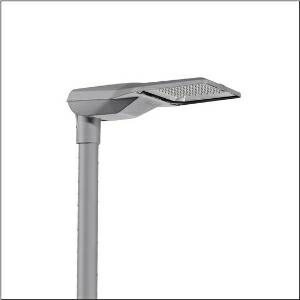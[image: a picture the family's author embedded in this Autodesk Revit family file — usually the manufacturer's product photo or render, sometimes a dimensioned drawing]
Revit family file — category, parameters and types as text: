
# Revit family: streetlight_sl_21_iq_midi___stw1_0a_5xe3e41d08nb_e017
name_source: partatom
category: Lighting Fixtures
units: mm (PartAtom-declared; Revit-internal decimal feet)

## family parameters
Cut with Voids When Loaded = No
Host = Face
Light Source = No
Part Type = Normal
Room Calculation Point = No
Round Connector Dimension = Use Diameter
Shared = No

## types (1)
- --- (1 x LED, 24250 lm, 155.5 W, 4000K)
    Apparent Load = 155 VA
    CIE Flux Codes = 39 75 98 100 100
    Color Rendering = 70
    Color Temperature = 4000K
    Default Elevation = 1800 mm
    Description = Streetlight SL 21 iQ midi, mast luminaire, primary light control with lens, of PMMA, primary optical cover: cover, of toughened safety glass, transparent, light distribution: STW1.0a, light emission: direct distribution, primary light characteristic: asymmetric, installation type: post-top, side-entry, LED, High Power LED, rated luminous flux: 24.250lm, luminous efficacy: 156lm/W, light colour: 740, colour temperature: 4000K, control gear: iQ-Comfort, control: Auto-Match, Temp-Guard, Lumen-Switch, Night-Set, Smart-Wire, Light-Fading, Desk-Remote (wireless, voltage-free reading and setting of iQ features in the workshop via application-optimized NFC function/RFID function), optimised constant luminous flux control (CLO 2.0), pre-setting: linear dimming characteristic, mains connection: 230..240V, AC, 50/60Hz, start of lifetime: 156W, end of service life: 162W, reduction: 69W, luminaire housing, of diecast aluminium, powder-coated, Siteco® metallic grey (DB 702S), corrosivity category C5 mid according to DIN EN ISO 12944, please order mast flange separately, inclination adjustable: 0°, 5°, 10°, 15°, sealing non-destructively replaceable, multi-level sealing system, length: 644mm, width: 335mm, height: 110mm, mast flange for spigot size: 42mm (side-entry): 5XC10008XM4, 60/48mm (side-entry/post-top): 5XC10108XM2, 76/60mm (side-entry/post-top): 5XC10108XM1, mounting height: 4..8m, protection rating (complete): IP66, insulation class (complete): insulation class II (safety insulation), certification: CE, ENEC, ENEC+, VDE, impact resistance: IK10, permissible operating ambient temperature for outdoor applications: -40..+50°C, standard-compliant lighting for roads and squares, packaging unit: 1 piece

Light Distribution: STW1.0a
    Height = 111 mm
    Lamp = 1 x LED
    Lamp Light Flux = 24250 lm
    Lamp Power = 155.5 W
    Lamp count = 1
    Length = 644 mm
    Luminous efficacy = 156 lm/W
    Manufacturer = Siteco
    ModVariant = No
    Model = 5XE3E41D08NB
    Number of Poles = 1
    OnlyDefault = Yes
    Power Factor = 1
    Product Name = Streetlight SL 21 iQ midi | STW1.0a
    Product group = mast luminaire | pylon top
    ProductGroupID = 6100
    Protection Class = Protection class II
    Protection Degree = IP 66
    RLX_Detail_Level = 1
    RLX_Emergency_Light_Flux = 0 lm
    RLX_Emergency_Type = 0
    RLX_Emergency_Type_DB = No
    RlxData = <blob elided: 27245 chars, md5=431fd354>
    Socket = socket
    Standby Power = 0 W
    System Light Flux = 24250 lm
    System Power = 155 W
    Type Comments = factory setting: luminous flux: 100 % | dim-lin: 254 | 823 mA
    Type Image = l_1004298.jpg
    URL = http://relux.com
    VarID = @adj_169844
    Voltage = 0 V
    Weight = 0.00 kg
    Width = 336 mm

## geometry (parser evidence)
native form markers: Blend x4, Sweep x12
no freeform markers — native parametric forms only
